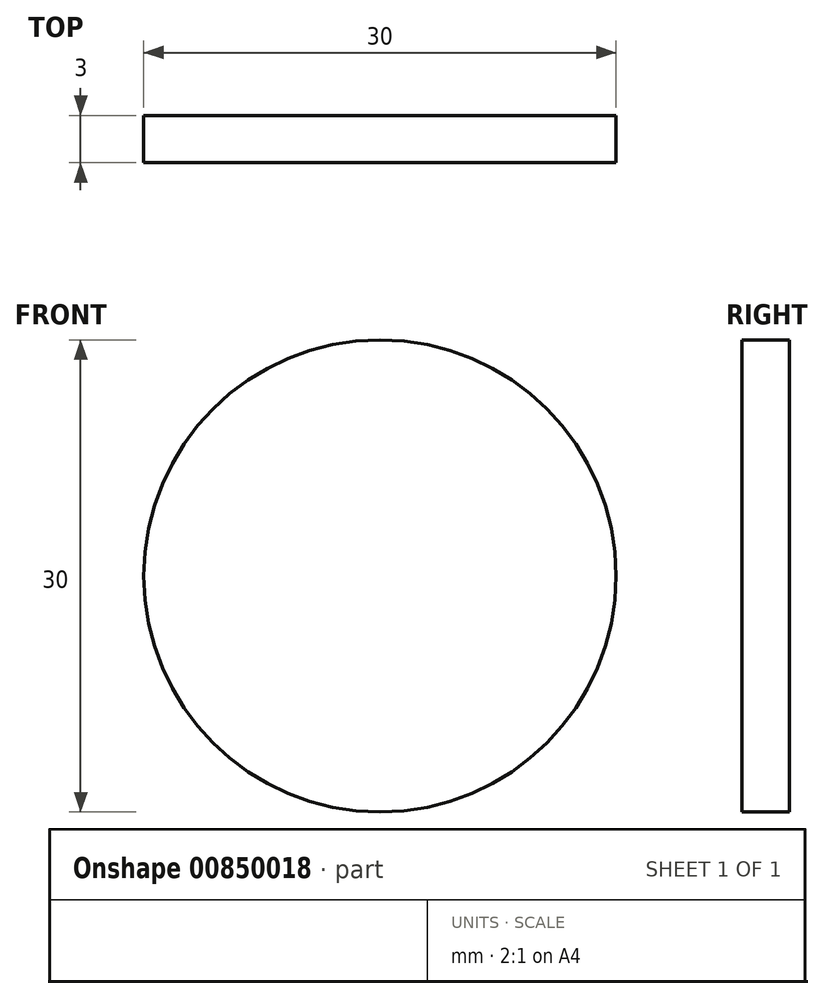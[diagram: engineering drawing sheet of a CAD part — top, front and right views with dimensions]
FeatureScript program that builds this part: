
annotation { "Feature Type Name" : "Feature", "Feature Type Description" : "" }
export const myFeature = defineFeature(function(context is Context, id is Id, definition is map)
    precondition{}
    {
        {
            var Q0;
            Q0=qCreatedBy(makeId("Front.planeOp"),FACE);
            var sketch = newSketch(context, id + "F0", { "sketchPlane" : qUnion([Q0])});
            skCircle(sketch, "E0", {"center": v(0, 0) * mm, "radius": 15 * mm});
            skSolve(sketch);
        }
        {
            var Q0;
            Q0=makeQuery(id+"F0.imprint","IMPRINT",FACE,{"disambiguationData":[TD([[makeQuery(id+"F0.imprint","IMPRINT",EDGE,{"derivedFrom":sQuery(id+"F0.wireOp",EDGE,"E0")}),1.0]])]});
            extrude(context, id + "F1", {"entities" : qUnion([Q0]), "depth" : 3 * mm, "offsetDistance" : 25 * mm});
        }
    });
